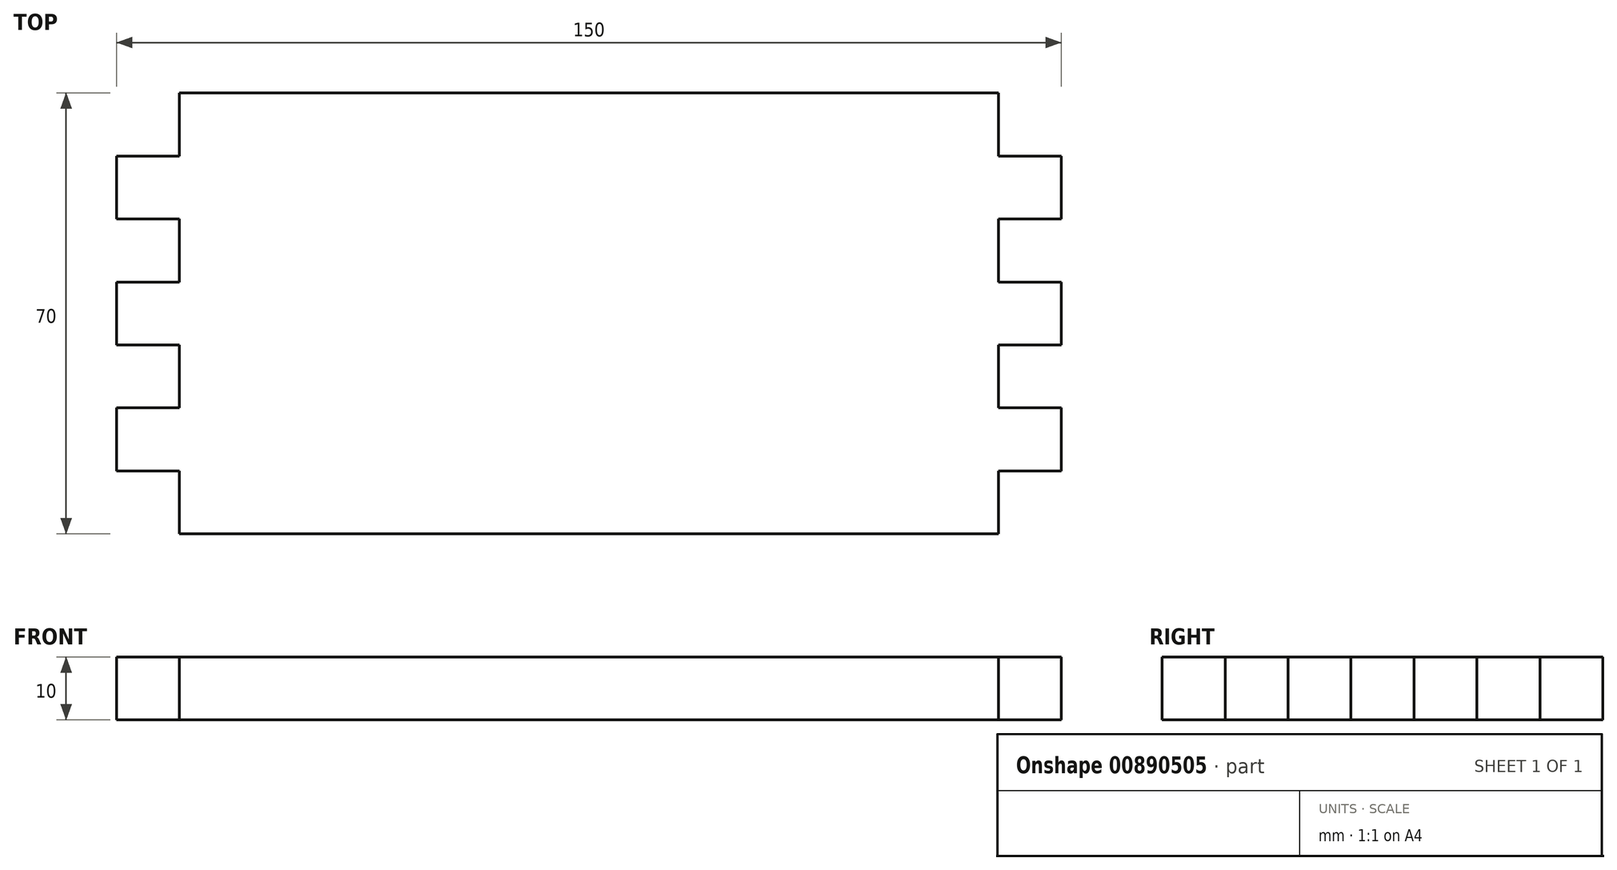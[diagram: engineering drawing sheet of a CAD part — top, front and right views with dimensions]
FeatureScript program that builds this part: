
annotation { "Feature Type Name" : "Feature", "Feature Type Description" : "" }
export const myFeature = defineFeature(function(context is Context, id is Id, definition is map)
    precondition{}
    {
        {
            var Q0;
            Q0=qCreatedBy(makeId("Top.planeOp"),FACE);
            var sketch = newSketch(context, id + "F0", { "sketchPlane" : qUnion([Q0])});
            skLineSegment(sketch, "E0.top", {"start": v(65, -45) * mm, "end": v(0, -45) * mm});
            skPoint(sketch, "E0.middle", {"position": v(0, 0) * mm});
            skLineSegment(sketch, "E1", {"start": v(65, 25) * mm, "end": v(65, 15) * mm});
            skLineSegment(sketch, "E2", {"start": v(65, 15) * mm, "end": v(75, 15) * mm});
            skLineSegment(sketch, "E3", {"start": v(75, 15) * mm, "end": v(75, 5) * mm});
            skLineSegment(sketch, "E4", {"start": v(75, 5) * mm, "end": v(65, 5) * mm});
            skLineSegment(sketch, "E5", {"start": v(65, 5) * mm, "end": v(65, -5) * mm});
            skLineSegment(sketch, "E6", {"start": v(65, -5) * mm, "end": v(75, -5) * mm});
            skLineSegment(sketch, "E7", {"start": v(75, -5) * mm, "end": v(75, -15) * mm});
            skLineSegment(sketch, "E8", {"start": v(75, -15) * mm, "end": v(65, -15) * mm});
            skLineSegment(sketch, "E9", {"start": v(65, -15) * mm, "end": v(65, -25) * mm});
            skLineSegment(sketch, "E10", {"start": v(65, -25) * mm, "end": v(75, -25) * mm});
            skLineSegment(sketch, "E11", {"start": v(75, -25) * mm, "end": v(75, -35) * mm});
            skLineSegment(sketch, "E12", {"start": v(75, -35) * mm, "end": v(65, -35) * mm});
            skLineSegment(sketch, "E13", {"start": v(65, -35) * mm, "end": v(65, -45) * mm});
            skPoint(sketch, "E0.right.end.orphan", {"position": v(-75, -45) * mm});
            skPoint(sketch, "E0.right.start.orphan", {"position": v(-75, 45) * mm});
            skLineSegment(sketch, "E14.MirrorCS", {"start": v(-75, -25) * mm, "end": v(-75, -35) * mm});
            skLineSegment(sketch, "E15.MirrorCS", {"start": v(-75, 15) * mm, "end": v(-75, 5) * mm});
            skLineSegment(sketch, "E16.MirrorCS", {"start": v(-75, -5) * mm, "end": v(-75, -15) * mm});
            skLineSegment(sketch, "E17.MirrorCS", {"start": v(-65, 5) * mm, "end": v(-65, -5) * mm});
            skLineSegment(sketch, "E18.MirrorCS", {"start": v(-65, -5) * mm, "end": v(-75, -5) * mm});
            skLineSegment(sketch, "E19.MirrorCS", {"start": v(-65, -45) * mm, "end": v(0, -45) * mm});
            skLineSegment(sketch, "E20.MirrorCS", {"start": v(-65, -35) * mm, "end": v(-65, -45) * mm});
            skLineSegment(sketch, "E21.MirrorCS", {"start": v(-75, -15) * mm, "end": v(-65, -15) * mm});
            skLineSegment(sketch, "E22.MirrorCS", {"start": v(-75, 5) * mm, "end": v(-65, 5) * mm});
            skLineSegment(sketch, "E23.MirrorCS", {"start": v(-65, -25) * mm, "end": v(-75, -25) * mm});
            skLineSegment(sketch, "E24.MirrorCS", {"start": v(-75, -35) * mm, "end": v(-65, -35) * mm});
            skLineSegment(sketch, "E25.MirrorCS", {"start": v(-65, 25) * mm, "end": v(-65, 15) * mm});
            skLineSegment(sketch, "E26.MirrorCS", {"start": v(-65, -15) * mm, "end": v(-65, -25) * mm});
            skLineSegment(sketch, "E27.MirrorCS", {"start": v(-65, 15) * mm, "end": v(-75, 15) * mm});
            skLineSegment(sketch, "E28", {"start": v(-65, 25) * mm, "end": v(65, 25) * mm});
            skPoint(sketch, "E0.left.start.orphan", {"position": v(75, 35) * mm});
            skSolve(sketch);
        }
        {
            var Q0;
            Q0=makeQuery(id+"F0.imprint","IMPRINT",FACE,{"disambiguationData":[TD([[makeQuery(id+"F0.imprint","IMPRINT",EDGE,{"derivedFrom":sQuery(id+"F0.wireOp",EDGE,"E0.top")}),-1.0]])]});
            extrude(context, id + "F1", {"entities" : qUnion([Q0]), "depth" : 10 * mm, "offsetDistance" : 25 * mm});
        }
    });
